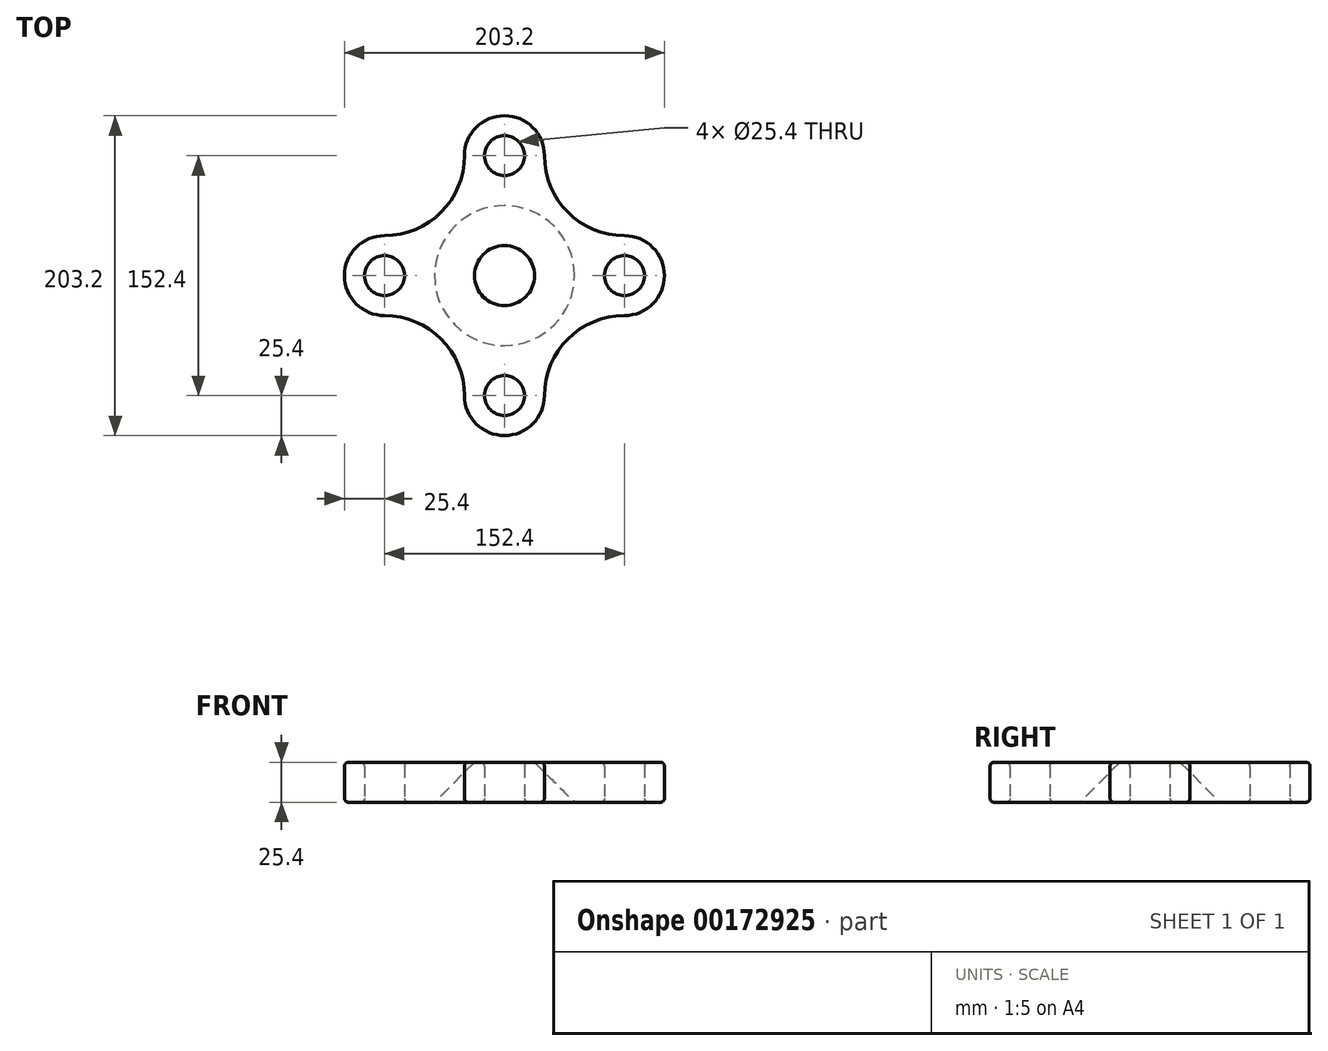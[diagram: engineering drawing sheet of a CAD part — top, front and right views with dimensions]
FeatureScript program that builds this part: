
annotation { "Feature Type Name" : "Feature", "Feature Type Description" : "" }
export const myFeature = defineFeature(function(context is Context, id is Id, definition is map)
    precondition{}
    {
        {
            var Q0;
            Q0=qCreatedBy(makeId("Top.planeOp"),FACE);
            var sketch = newSketch(context, id + "F0", { "sketchPlane" : qUnion([Q0])});
            skArc(sketch, "E0", {"start": v(25.4, 76.2) * mm, "mid": v(0, 101.6) * mm, "end": v(-25.4, 76.2) * mm});
            skCircle(sketch, "E1", {"center": v(0, 76.2) * mm, "radius": 12.7 * mm});
            skArc(sketch, "E2", {"start": v(76.2, 25.4) * mm, "mid": v(101.6, 0) * mm, "end": v(76.2, -25.4) * mm});
            skArc(sketch, "E3", {"start": v(25.4, -76.2) * mm, "mid": v(0, -101.6) * mm, "end": v(-25.4, -76.2) * mm});
            skArc(sketch, "E4", {"start": v(-76.2, 25.4) * mm, "mid": v(-101.6, 0) * mm, "end": v(-76.2, -25.4) * mm});
            skCircle(sketch, "E5", {"center": v(-76.2, 0) * mm, "radius": 12.7 * mm});
            skCircle(sketch, "E6", {"center": v(76.2, 0) * mm, "radius": 12.7 * mm});
            skCircle(sketch, "E7", {"center": v(0, -76.2) * mm, "radius": 12.7 * mm});
            skArc(sketch, "E8", {"start": v(25.4, 76.2) * mm, "mid": v(40.28, 40.28) * mm, "end": v(76.2, 25.4) * mm});
            skArc(sketch, "E9", {"start": v(-76.2, 25.4) * mm, "mid": v(-40.28, 40.28) * mm, "end": v(-25.4, 76.2) * mm});
            skArc(sketch, "E10", {"start": v(-25.4, -76.2) * mm, "mid": v(-40.28, -40.28) * mm, "end": v(-76.2, -25.4) * mm});
            skArc(sketch, "E11", {"start": v(76.2, -25.4) * mm, "mid": v(40.28, -40.28) * mm, "end": v(25.4, -76.2) * mm});
            skCircle(sketch, "E12", {"center": v(0, 0) * mm, "radius": 76.2 * mm, "construction": true});
            skSolve(sketch);
        }
        {
            var Q0;
            Q0=makeQuery(id+"F0.imprint","IMPRINT",FACE,{"disambiguationData":[TD([[makeQuery(id+"F0.imprint","IMPRINT",EDGE,{"derivedFrom":sQuery(id+"F0.wireOp",EDGE,"E0")}),1.0]])]});
            extrude(context, id + "F1", {"entities" : qUnion([Q0]), "depth" : 25.4 * mm});
        }
        {
            var Q0;
            Q0=makeQuery(id+"F1.opExtrude","CAP_FACE",FACE,{"disambiguationData":[OSD([sQuery(id+"F0.wireOp",EDGE,"E0"),sQuery(id+"F0.wireOp",EDGE,"E1"),sQuery(id+"F0.wireOp",EDGE,"E2"),sQuery(id+"F0.wireOp",EDGE,"E3"),sQuery(id+"F0.wireOp",EDGE,"E4"),sQuery(id+"F0.wireOp",EDGE,"E5"),sQuery(id+"F0.wireOp",EDGE,"E6"),sQuery(id+"F0.wireOp",EDGE,"E7"),sQuery(id+"F0.wireOp",EDGE,"E8"),sQuery(id+"F0.wireOp",EDGE,"E9"),sQuery(id+"F0.wireOp",EDGE,"E10"),sQuery(id+"F0.wireOp",EDGE,"E11")])],"isStart":false});
            var Q1;
            Q1=makeQuery(id+"F1.opExtrude","CAP_FACE",FACE,{"disambiguationData":[OSD([sQuery(id+"F0.wireOp",EDGE,"E0"),sQuery(id+"F0.wireOp",EDGE,"E1"),sQuery(id+"F0.wireOp",EDGE,"E2"),sQuery(id+"F0.wireOp",EDGE,"E3"),sQuery(id+"F0.wireOp",EDGE,"E4"),sQuery(id+"F0.wireOp",EDGE,"E5"),sQuery(id+"F0.wireOp",EDGE,"E6"),sQuery(id+"F0.wireOp",EDGE,"E7"),sQuery(id+"F0.wireOp",EDGE,"E8"),sQuery(id+"F0.wireOp",EDGE,"E9"),sQuery(id+"F0.wireOp",EDGE,"E10"),sQuery(id+"F0.wireOp",EDGE,"E11")])],"isStart":true});
            fillet(context, id + "F2", {"entities" : qUnion([Q0, Q1]), "radius" : 2.54 * mm, "tangentPropagation" : true, "allowEdgeOverflow" : false});
        }
        {
            var Q0;
            Q0=qCreatedBy(makeId("Front.planeOp"),FACE);
            var sketch = newSketch(context, id + "F3", { "sketchPlane" : qUnion([Q0])});
            skLineSegment(sketch, "E13", {"start": v(0, 0) * mm, "end": v(0, 25.4) * mm});
            skLineSegment(sketch, "E14", {"start": v(0, 25.4) * mm, "end": v(-19.05, 25.4) * mm});
            skLineSegment(sketch, "E15", {"start": v(-19.05, 25.4) * mm, "end": v(-44.45, 0) * mm});
            skLineSegment(sketch, "E16", {"start": v(-44.45, 0) * mm, "end": v(0, 0) * mm});
            skLineSegment(sketch, "E17", {"start": v(0, 0) * mm, "end": v(0, -17) * mm, "construction": true});
            skSolve(sketch);
        }
        {
            var Q0;
            Q0 = qSketchRegion(id + "F3", true);
            var Q1;
            Q1=sQuery(id+"F3.wireOp",EDGE,"E17");
            revolve(context, id + "F4", {"operationType" : NewBodyOperationType.REMOVE, "entities" : qUnion([Q0]), "axis" : qUnion([Q1]), "revolveType" : RevolveType.FULL});
        }
    });
